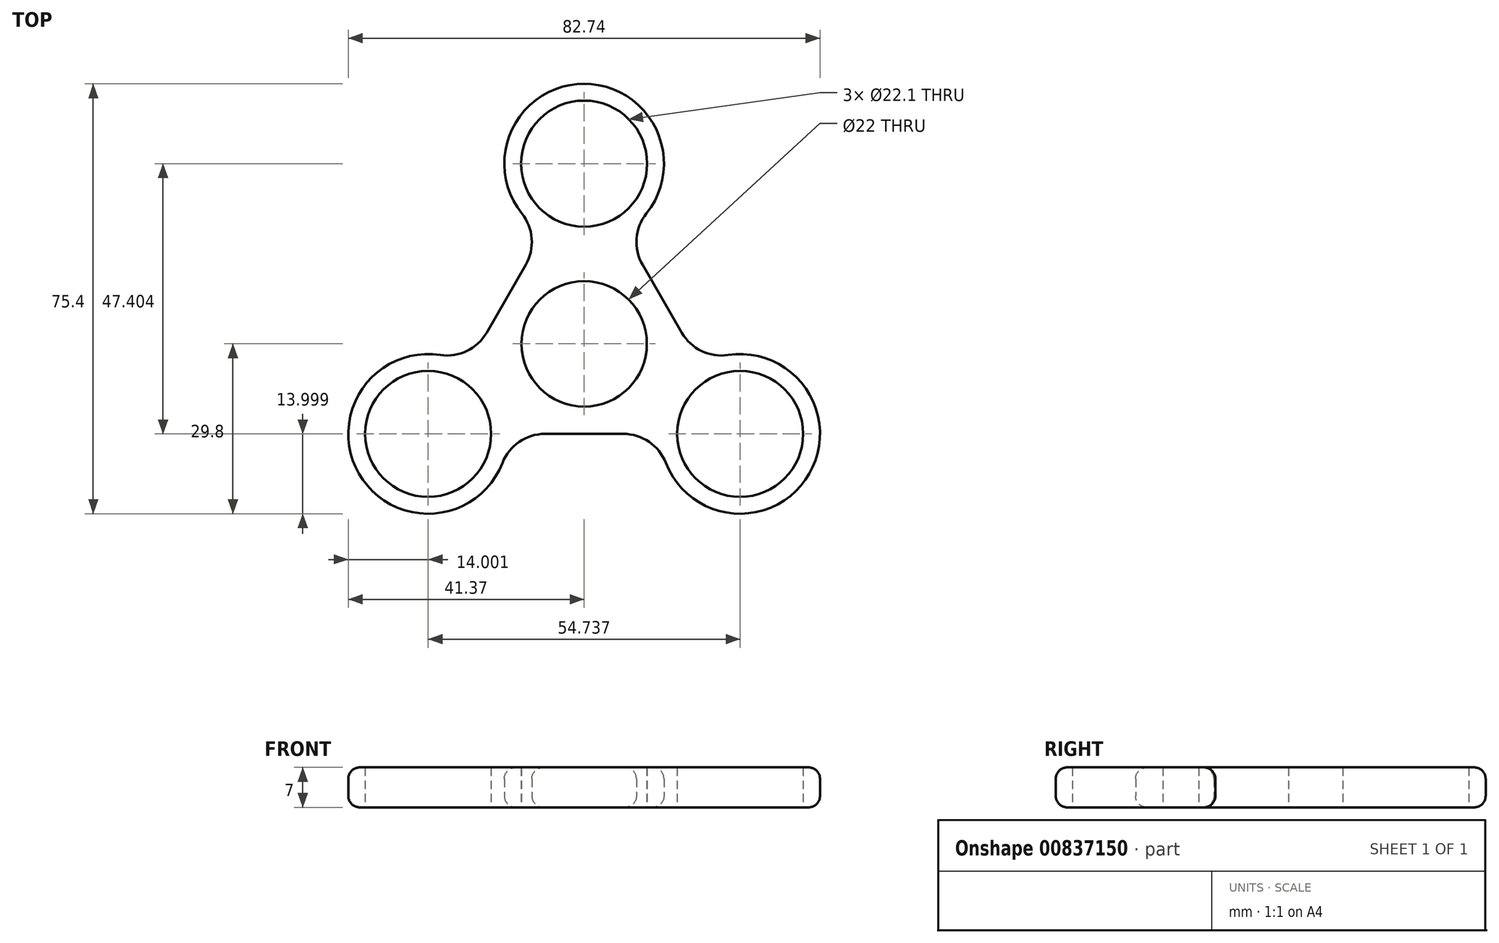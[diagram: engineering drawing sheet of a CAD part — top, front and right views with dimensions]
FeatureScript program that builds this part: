
annotation { "Feature Type Name" : "Feature", "Feature Type Description" : "" }
export const myFeature = defineFeature(function(context is Context, id is Id, definition is map)
    precondition{}
    {
        {
            var Q0;
            Q0=qCreatedBy(makeId("Top.planeOp"),FACE);
            var sketch = newSketch(context, id + "F0", { "sketchPlane" : qUnion([Q0])});
            skCircle(sketch, "E0", {"center": v(0, 31.6) * mm, "radius": 11.05 * mm});
            skCircle(sketch, "E1.1.0", {"center": v(-27.37, -15.8) * mm, "radius": 11.05 * mm});
            skCircle(sketch, "E1.2.0", {"center": v(27.37, -15.8) * mm, "radius": 11.05 * mm});
            skPoint(sketch, "E1.center", {"position": v(0, 0) * mm});
            skCircle(sketch, "E2", {"center": v(0, 31.6) * mm, "radius": 14 * mm});
            skCircle(sketch, "E3.1.0", {"center": v(-27.37, -15.8) * mm, "radius": 14 * mm});
            skCircle(sketch, "E3.2.0", {"center": v(27.37, -15.8) * mm, "radius": 14 * mm});
            skCircle(sketch, "E4", {"center": v(0, 0) * mm, "radius": 11 * mm});
            skCircle(sketch, "E5", {"center": v(0, 0) * mm, "radius": 14 * mm, "construction": true});
            skLineSegment(sketch, "E6", {"start": v(-27.37, -15.8) * mm, "end": v(0, 31.6) * mm});
            skLineSegment(sketch, "E7", {"start": v(0, 31.6) * mm, "end": v(27.37, -15.8) * mm});
            skLineSegment(sketch, "E8", {"start": v(27.37, -15.8) * mm, "end": v(-27.37, -15.8) * mm});
            skPoint(sketch, "E9", {"position": v(0, 45.6) * mm});
            skSolve(sketch);
        }
        {
            var Q0;
            Q0=qSketchRegion(id+"F0",true);
            extrude(context, id + "F1", {"entities" : qUnion([Q0]), "endBound" : BoundingType.SYMMETRIC, "depth" : 7 * mm, "offsetDistance" : 25 * mm});
        }
        {
            var Q0;
            Q0=makeQuery(id+"F1.opExtrude","SWEPT_EDGE",EDGE,{"disambiguationData":[OSD([sQuery(id+"F0.wireOp",EDGE,"E3.2.0"),sQuery(id+"F0.wireOp",EDGE,"zSg69FSz-ja27-GQGE-MR0P-PLYQZ15IPlXa")])]});
            var Q1;
            Q1=makeQuery(id+"F1.opExtrude","SWEPT_EDGE",EDGE,{"disambiguationData":[OSD([sQuery(id+"F0.wireOp",EDGE,"E2"),sQuery(id+"F0.wireOp",EDGE,"zSg69FSz-ja27-GQGE-MR0P-PLYQZ15IPlXa")])]});
            var Q2;
            Q2=makeQuery(id+"F1.opExtrude","SWEPT_EDGE",EDGE,{"disambiguationData":[OSD([sQuery(id+"F0.wireOp",EDGE,"E2"),sQuery(id+"F0.wireOp",EDGE,"oBNQ3VcD-oVfM-tYSh-CwtA-rd2oLKiVvI6k")])]});
            var Q3;
            Q3=makeQuery(id+"F1.opExtrude","SWEPT_EDGE",EDGE,{"disambiguationData":[OSD([sQuery(id+"F0.wireOp",EDGE,"E3.2.0"),sQuery(id+"F0.wireOp",EDGE,"oS4GqZWx-UiGZ-MHNm-b1dr-cg6UlFnWGaa9")])]});
            var Q4;
            Q4=makeQuery(id+"F1.opExtrude","SWEPT_EDGE",EDGE,{"disambiguationData":[OSD([sQuery(id+"F0.wireOp",EDGE,"E3.1.0"),sQuery(id+"F0.wireOp",EDGE,"oBNQ3VcD-oVfM-tYSh-CwtA-rd2oLKiVvI6k")])]});
            var Q5;
            Q5=makeQuery(id+"F1.opExtrude","SWEPT_EDGE",EDGE,{"disambiguationData":[OSD([sQuery(id+"F0.wireOp",EDGE,"E3.1.0"),sQuery(id+"F0.wireOp",EDGE,"oS4GqZWx-UiGZ-MHNm-b1dr-cg6UlFnWGaa9")])]});
            fillet(context, id + "F2", {"entities" : qUnion([Q0, Q1, Q2, Q3, Q4, Q5]), "radius" : 8 * mm, "tangentPropagation" : true, "allowEdgeOverflow" : false});
        }
        {
            var Q0;
            Q0=makeQuery(id+"F1.opExtrude","CAP_EDGE",EDGE,{"disambiguationData":[OSD([sQuery(id+"F0.wireOp",EDGE,"E3.1.0")])],"isStart":false});
            var Q1;
            Q1=makeQuery(id+"F1.opExtrude","CAP_EDGE",EDGE,{"disambiguationData":[OSD([sQuery(id+"F0.wireOp",EDGE,"E3.1.0")])],"isStart":true});
            fillet(context, id + "F3", {"entities" : qUnion([Q0, Q1]), "radius" : 2 * mm, "tangentPropagation" : true, "allowEdgeOverflow" : false});
        }
    });
